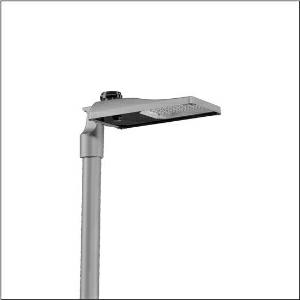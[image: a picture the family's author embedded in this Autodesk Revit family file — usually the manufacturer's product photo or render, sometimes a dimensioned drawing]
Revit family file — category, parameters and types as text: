
# Revit family: streetlight_sl_31_mini___st1_0a_5xh6d3bm08ga_d2dc
name_source: partatom
category: Lighting Fixtures
units: mm (PartAtom-declared; Revit-internal decimal feet)

## family parameters
Cut with Voids When Loaded = No
Host = Face
Light Source = No
Part Type = Normal
Room Calculation Point = No
Round Connector Dimension = Use Diameter
Shared = No

## types (1)
- --- (1 x LED, 5880 lm, 39.3 W, 3000K)
    Apparent Load = 39 VA
    CIE Flux Codes = 37 72 97 100 100
    Color Rendering = 70
    Color Temperature = 3000K
    Default Elevation = 1800 mm
    Description = Streetlight SL 31 mini NEMA (7pin) mast luminaire for post-top, side-entry; light control with lens of PMMA; light distribution: ST1.0a, direct asymmetric distribution, for standard-compliant lighting for roads and squares; LED: luminous flux: 5.880lm, light colour: 730, colour temperature: 3000K; luminous efficacy: 149,6lm/W; control: pre-setting: linear dimming characteristic, flexible luminous flux parameterisation, time-dependent luminous flux control, constant luminous flux control, intelligent temperature release in ECG and LED module, overheat protection; luminaire housing, of diecast aluminium, SITECO metallic grey (DB 702S), corrosivity category C5 high according to DIN EN ISO 12944; cover of toughened safety glass, transparent, opened without tools; mast flange of diecast aluminium, SITECO metallic grey (DB 702S), spigot size: 76/60mm, mast flange included unmounted; cable length: 6,5m, connection cable pre-assembled; mains connection: 220..240V, AC, 50/60Hz; power consumption (at start of service life): 39,3W / (at end of service life): 40,7W / (with reduced operation 50%): 18,1W; protection rating (complete): IP66; insulation class (complete): insulation class I (protective earthing); impact resistance: IK09; certification: CE, ENEC, ENEC+, VDE, UKCA; permissible operating ambient temperature for outdoor applications: -40..+50°C; packaging unit: 1 piece

Light Distribution: ST1.0a
    Height = 76 mm
    Lamp = 1 x LED
    Lamp Light Flux = 5880 lm
    Lamp Power = 39.3 W
    Lamp count = 1
    Length = 547 mm
    Luminous efficacy = 150 lm/W
    Manufacturer = Siteco
    ModVariant = No
    Model = 5XH6D3BM08GA
    Number of Poles = 1
    OnlyDefault = Yes
    Power Factor = 1
    Product Name = Streetlight SL 31 mini | ST1.0a
    Product group = mast luminaire | pylon top
    ProductGroupID = 6100
    Protection Class = Protection class I
    Protection Degree = IP 66
    RLX_Detail_Level = 1
    RLX_Emergency_Light_Flux = 0 lm
    RLX_Emergency_Type = 0
    RLX_Emergency_Type_DB = No
    RlxData = <blob elided: 40353 chars, md5=62aff176>
    Socket = socket
    Standby Power = 0 W
    System Light Flux = 5880 lm
    System Power = 39 W
    Type Comments = factory setting: luminous flux: 100 % | dim-lin: 254 | 798 mA
    Type Image = l_1300324.jpg
    URL = http://relux.com
    VarID = @adj_060349
    Voltage = 0 V
    Weight = 0.00 kg
    Width = 265 mm

## geometry (parser evidence)
native form markers: Blend x4, Sweep x9
no freeform markers — native parametric forms only
